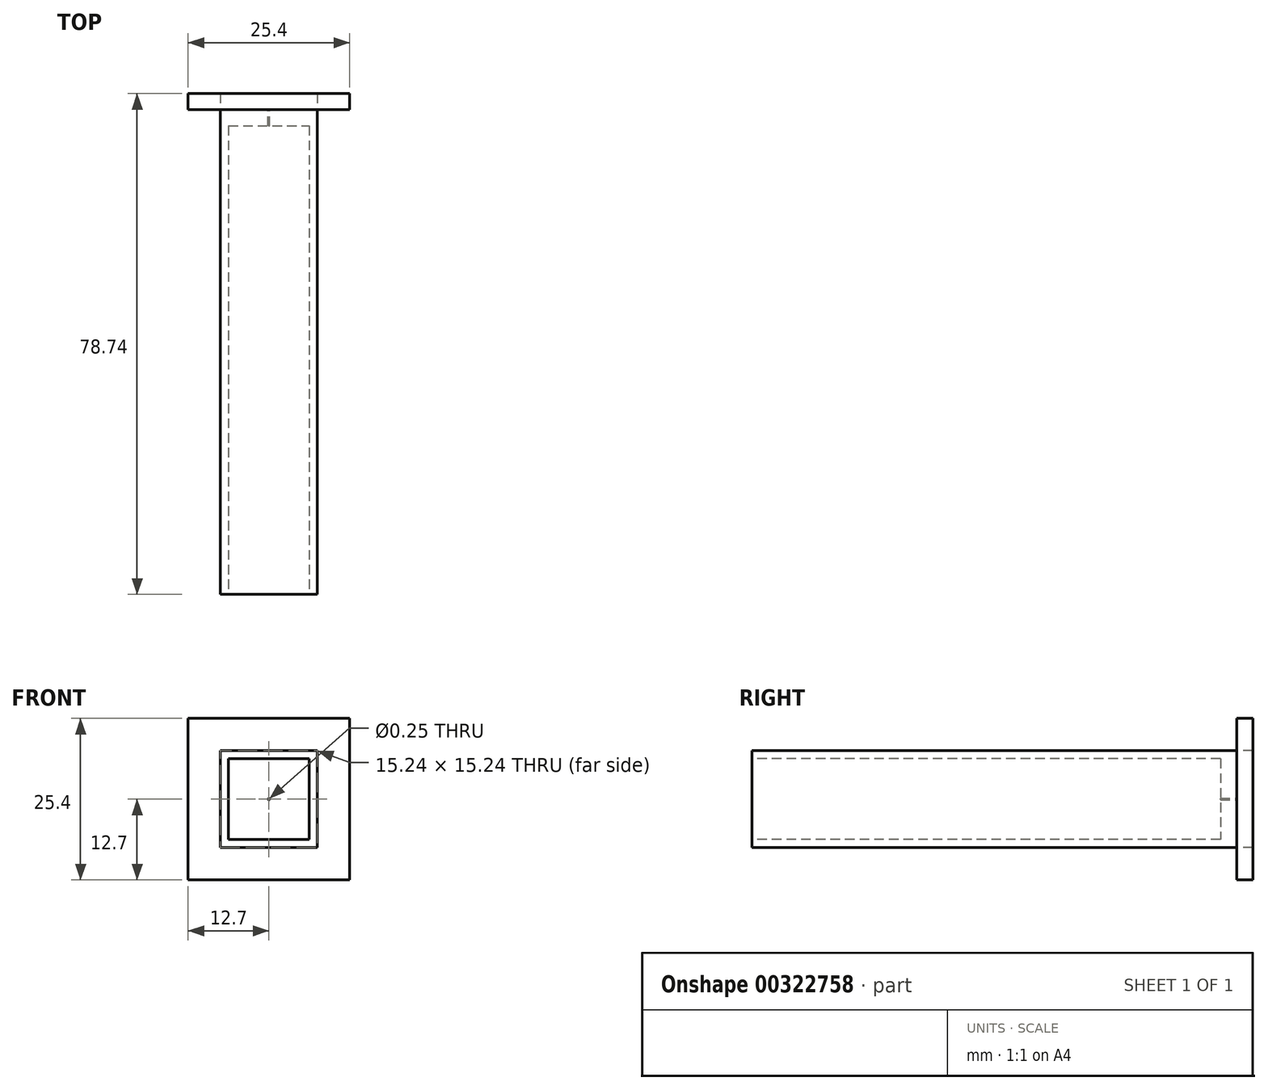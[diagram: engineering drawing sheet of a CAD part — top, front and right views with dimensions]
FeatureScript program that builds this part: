
annotation { "Feature Type Name" : "Feature", "Feature Type Description" : "" }
export const myFeature = defineFeature(function(context is Context, id is Id, definition is map)
    precondition{}
    {
        {
            var Q0;
            Q0=qCreatedBy(makeId("Front.planeOp"),FACE);
            var sketch = newSketch(context, id + "F0", { "sketchPlane" : qUnion([Q0])});
            skLineSegment(sketch, "E0.bottom", {"start": v(-12.7, 12.7) * mm, "end": v(12.7, 12.7) * mm});
            skLineSegment(sketch, "E0.top", {"start": v(-12.7, -12.7) * mm, "end": v(12.7, -12.7) * mm});
            skLineSegment(sketch, "E0.left", {"start": v(-12.7, 12.7) * mm, "end": v(-12.7, -12.7) * mm});
            skLineSegment(sketch, "E0.right", {"start": v(12.7, 12.7) * mm, "end": v(12.7, -12.7) * mm});
            skSolve(sketch);
        }
        {
            var Q0;
            Q0 = qSketchRegion(id + "F0", true);
            extrude(context, id + "F1", {"entities" : qUnion([Q0]), "depth" : 2.54 * mm});
        }
        {
            var Q0;
            Q0=makeQuery(id+"F1.opExtrude","CAP_FACE",FACE,{"disambiguationData":[OSD([sQuery(id+"F0.wireOp",EDGE,"E0.bottom"),sQuery(id+"F0.wireOp",EDGE,"E0.top"),sQuery(id+"F0.wireOp",EDGE,"E0.left"),sQuery(id+"F0.wireOp",EDGE,"E0.right")])],"isStart":false});
            var sketch = newSketch(context, id + "F2", { "sketchPlane" : qUnion([Q0])});
            skLineSegment(sketch, "E1.bottom", {"start": v(-7.62, 7.62) * mm, "end": v(7.62, 7.62) * mm});
            skLineSegment(sketch, "E1.top", {"start": v(-7.62, -7.62) * mm, "end": v(7.62, -7.62) * mm});
            skLineSegment(sketch, "E1.left", {"start": v(-7.62, 7.62) * mm, "end": v(-7.62, -7.62) * mm});
            skLineSegment(sketch, "E1.right", {"start": v(7.62, 7.62) * mm, "end": v(7.62, -7.62) * mm});
            skSolve(sketch);
        }
        {
            var Q0;
            Q0=makeQuery(id+"F2.imprint","IMPRINT",FACE,{"disambiguationData":[TD([[makeQuery(id+"F2.imprint","IMPRINT",EDGE,{"derivedFrom":sQuery(id+"F2.wireOp",EDGE,"E1.bottom")}),-1.0]])]});
            extrude(context, id + "F3", {"entities" : qUnion([Q0]), "operationType" : NewBodyOperationType.REMOVE, "endBound" : BoundingType.THROUGH_ALL, "oppositeDirection" : true, "depth" : 25.4 * mm});
        }
        {
            var Q0;
            Q0=makeQuery(id+"F1.opExtrude","CAP_FACE",FACE,{"disambiguationData":[OSD([sQuery(id+"F0.wireOp",EDGE,"E0.bottom"),sQuery(id+"F0.wireOp",EDGE,"E0.top"),sQuery(id+"F0.wireOp",EDGE,"E0.left"),sQuery(id+"F0.wireOp",EDGE,"E0.right")])],"isStart":false});
            var sketch = newSketch(context, id + "F4", { "sketchPlane" : qUnion([Q0])});
            skLineSegment(sketch, "E2.bottom", {"start": v(-7.62, 7.62) * mm, "end": v(7.62, 7.62) * mm});
            skLineSegment(sketch, "E2.top", {"start": v(-7.62, -7.62) * mm, "end": v(7.62, -7.62) * mm});
            skLineSegment(sketch, "E2.left", {"start": v(-7.62, 7.62) * mm, "end": v(-7.62, -7.62) * mm});
            skLineSegment(sketch, "E2.right", {"start": v(7.62, 7.62) * mm, "end": v(7.62, -7.62) * mm});
            skSolve(sketch);
        }
        {
            var Q0;
            Q0=makeQuery(id+"F4.imprint","IMPRINT",FACE,{"disambiguationData":[TD([[makeQuery(id+"F4.imprint","IMPRINT",EDGE,{"derivedFrom":sQuery(id+"F4.wireOp",EDGE,"E2.bottom")}),-1.0]])]});
            extrude(context, id + "F5", {"entities" : qUnion([Q0]), "depth" : 76.2 * mm});
        }
        {
            var Q0;
            Q0=makeQuery(id+"F5.opExtrude","CAP_FACE",FACE,{"disambiguationData":[OSD([sQuery(id+"F4.wireOp",EDGE,"E2.bottom"),sQuery(id+"F4.wireOp",EDGE,"E2.top"),sQuery(id+"F4.wireOp",EDGE,"E2.left"),sQuery(id+"F4.wireOp",EDGE,"E2.right")])],"isStart":false});
            var sketch = newSketch(context, id + "F6", { "sketchPlane" : qUnion([Q0])});
            skLineSegment(sketch, "E3.bottom", {"start": v(-6.35, 6.35) * mm, "end": v(6.35, 6.35) * mm});
            skLineSegment(sketch, "E3.top", {"start": v(-6.35, -6.35) * mm, "end": v(6.35, -6.35) * mm});
            skLineSegment(sketch, "E3.left", {"start": v(-6.35, 6.35) * mm, "end": v(-6.35, -6.35) * mm});
            skLineSegment(sketch, "E3.right", {"start": v(6.35, 6.35) * mm, "end": v(6.35, -6.35) * mm});
            skSolve(sketch);
        }
        {
            var Q0;
            Q0 = qSketchRegion(id + "F6", true);
            extrude(context, id + "F7", {"entities" : qUnion([Q0]), "operationType" : NewBodyOperationType.REMOVE, "oppositeDirection" : true, "depth" : 73.66 * mm});
        }
        {
            var Q0;
            Q0=makeQuery(id+"F5.opExtrude","CAP_FACE",FACE,{"disambiguationData":[OSD([sQuery(id+"F4.wireOp",EDGE,"E2.bottom"),sQuery(id+"F4.wireOp",EDGE,"E2.top"),sQuery(id+"F4.wireOp",EDGE,"E2.left"),sQuery(id+"F4.wireOp",EDGE,"E2.right")])],"isStart":true});
            var sketch = newSketch(context, id + "F8", { "sketchPlane" : qUnion([Q0])});
            skCircle(sketch, "E4", {"center": v(0, 0) * mm, "radius": 0.13 * mm});
            skSolve(sketch);
        }
        {
            var Q0;
            Q0 = qSketchRegion(id + "F8", true);
            extrude(context, id + "F9", {"entities" : qUnion([Q0]), "operationType" : NewBodyOperationType.REMOVE, "endBound" : BoundingType.THROUGH_ALL, "oppositeDirection" : true, "depth" : 25.4 * mm});
        }
    });
